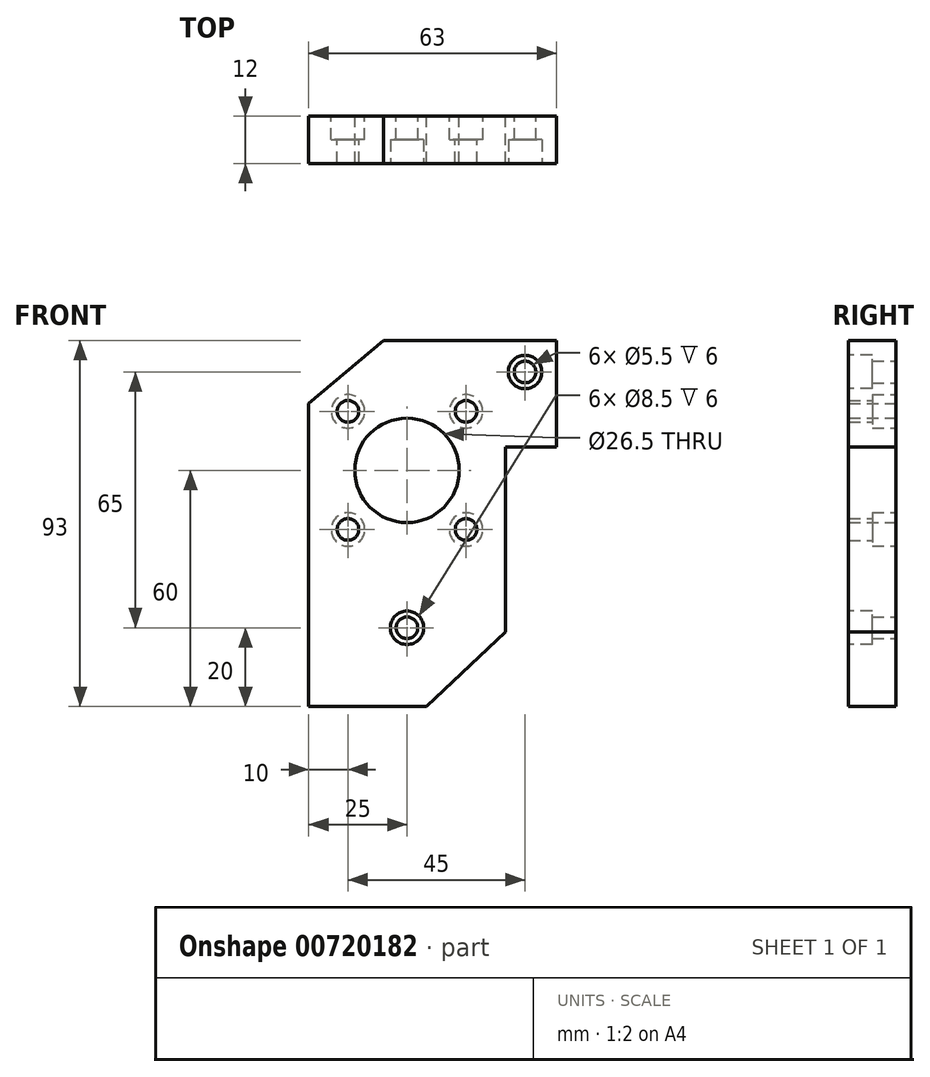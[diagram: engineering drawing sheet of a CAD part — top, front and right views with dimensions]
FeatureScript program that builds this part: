
annotation { "Feature Type Name" : "Feature", "Feature Type Description" : "" }
export const myFeature = defineFeature(function(context is Context, id is Id, definition is map)
    precondition{}
    {
        {
            var Q0;
            Q0=qCreatedBy(makeId("Front.planeOp"),FACE);
            var sketch = newSketch(context, id + "F0", { "sketchPlane" : qUnion([Q0])});
            skLineSegment(sketch, "E0", {"start": v(0, 77) * mm, "end": v(0, 0) * mm});
            skLineSegment(sketch, "E1", {"start": v(0, 0) * mm, "end": v(30, 0) * mm});
            skLineSegment(sketch, "E2", {"start": v(30, 0) * mm, "end": v(50, 19) * mm});
            skLineSegment(sketch, "E3", {"start": v(50, 19) * mm, "end": v(50, 66) * mm});
            skLineSegment(sketch, "E4", {"start": v(50, 66) * mm, "end": v(63, 66) * mm});
            skLineSegment(sketch, "E5", {"start": v(63, 66) * mm, "end": v(63, 93) * mm});
            skLineSegment(sketch, "E6", {"start": v(63, 93) * mm, "end": v(19, 93) * mm});
            skLineSegment(sketch, "E7", {"start": v(19, 93) * mm, "end": v(0, 77) * mm});
            skCircle(sketch, "E8", {"center": v(25, 60) * mm, "radius": 13.25 * mm});
            skCircle(sketch, "E9", {"center": v(25, 20) * mm, "radius": 2.75 * mm});
            skCircle(sketch, "E10", {"center": v(55, 85) * mm, "radius": 2.75 * mm});
            skCircle(sketch, "E11", {"center": v(10, 75) * mm, "radius": 2.75 * mm});
            skCircle(sketch, "E12.0.1.0", {"center": v(10, 45) * mm, "radius": 2.75 * mm});
            skCircle(sketch, "E12.1.0.0", {"center": v(40, 75) * mm, "radius": 2.75 * mm});
            skCircle(sketch, "E12.1.1.0", {"center": v(40, 45) * mm, "radius": 2.75 * mm});
            skLineSegment(sketch, "E12.direction1", {"start": v(10, 75) * mm, "end": v(40, 75) * mm, "construction": true});
            skLineSegment(sketch, "E12.direction2", {"start": v(10, 75) * mm, "end": v(10, 45) * mm, "construction": true});
            skSolve(sketch);
        }
        {
            var Q0;
            Q0=makeQuery(id+"F0.imprint","IMPRINT",FACE,{"disambiguationData":[TD([[makeQuery(id+"F0.imprint","IMPRINT",EDGE,{"derivedFrom":sQuery(id+"F0.wireOp",EDGE,"E0")}),1.0]])]});
            extrude(context, id + "F1", {"entities" : qUnion([Q0]), "depth" : 12 * mm, "offsetDistance" : 25 * mm});
        }
        {
            var Q0;
            Q0=makeQuery(id+"F1.opExtrude","CAP_FACE",FACE,{"disambiguationData":[OSD([sQuery(id+"F0.wireOp",EDGE,"E0"),sQuery(id+"F0.wireOp",EDGE,"E1"),sQuery(id+"F0.wireOp",EDGE,"E2"),sQuery(id+"F0.wireOp",EDGE,"E3"),sQuery(id+"F0.wireOp",EDGE,"E4"),sQuery(id+"F0.wireOp",EDGE,"E5"),sQuery(id+"F0.wireOp",EDGE,"E6"),sQuery(id+"F0.wireOp",EDGE,"E7"),sQuery(id+"F0.wireOp",EDGE,"E8"),sQuery(id+"F0.wireOp",EDGE,"E9"),sQuery(id+"F0.wireOp",EDGE,"E10"),sQuery(id+"F0.wireOp",EDGE,"E11"),sQuery(id+"F0.wireOp",EDGE,"E12.0.1.0"),sQuery(id+"F0.wireOp",EDGE,"E12.1.0.0"),sQuery(id+"F0.wireOp",EDGE,"E12.1.1.0")])],"isStart":false});
            var sketch = newSketch(context, id + "F2", { "sketchPlane" : qUnion([Q0])});
            skCircle(sketch, "E13", {"center": v(55, 85) * mm, "radius": 4.25 * mm});
            skCircle(sketch, "E14", {"center": v(25, 20) * mm, "radius": 4.25 * mm});
            skSolve(sketch);
        }
        {
            var Q0;
            Q0 = qSketchRegion(id + "F2", true);
            extrude(context, id + "F3", {"entities" : qUnion([Q0]), "operationType" : NewBodyOperationType.REMOVE, "oppositeDirection" : true, "depth" : 6 * mm, "offsetDistance" : 25 * mm});
        }
        {
            var Q0;
            Q0=makeQuery(id+"F1.opExtrude","CAP_FACE",FACE,{"disambiguationData":[OSD([sQuery(id+"F0.wireOp",EDGE,"E0"),sQuery(id+"F0.wireOp",EDGE,"E1"),sQuery(id+"F0.wireOp",EDGE,"E2"),sQuery(id+"F0.wireOp",EDGE,"E3"),sQuery(id+"F0.wireOp",EDGE,"E4"),sQuery(id+"F0.wireOp",EDGE,"E5"),sQuery(id+"F0.wireOp",EDGE,"E6"),sQuery(id+"F0.wireOp",EDGE,"E7"),sQuery(id+"F0.wireOp",EDGE,"E8"),sQuery(id+"F0.wireOp",EDGE,"E9"),sQuery(id+"F0.wireOp",EDGE,"E10"),sQuery(id+"F0.wireOp",EDGE,"E11"),sQuery(id+"F0.wireOp",EDGE,"E12.0.1.0"),sQuery(id+"F0.wireOp",EDGE,"E12.1.0.0"),sQuery(id+"F0.wireOp",EDGE,"E12.1.1.0")])],"isStart":true});
            var sketch = newSketch(context, id + "F4", { "sketchPlane" : qUnion([Q0])});
            skCircle(sketch, "E15", {"center": v(-10, 75) * mm, "radius": 4.25 * mm});
            skCircle(sketch, "E16", {"center": v(-40, 75) * mm, "radius": 4.25 * mm});
            skCircle(sketch, "E17", {"center": v(-40, 45) * mm, "radius": 4.25 * mm});
            skCircle(sketch, "E18", {"center": v(-10, 45) * mm, "radius": 4.25 * mm});
            skSolve(sketch);
        }
        {
            var Q0;
            Q0 = qSketchRegion(id + "F4", true);
            extrude(context, id + "F5", {"entities" : qUnion([Q0]), "operationType" : NewBodyOperationType.REMOVE, "oppositeDirection" : true, "depth" : 6 * mm, "offsetDistance" : 25 * mm});
        }
    });
